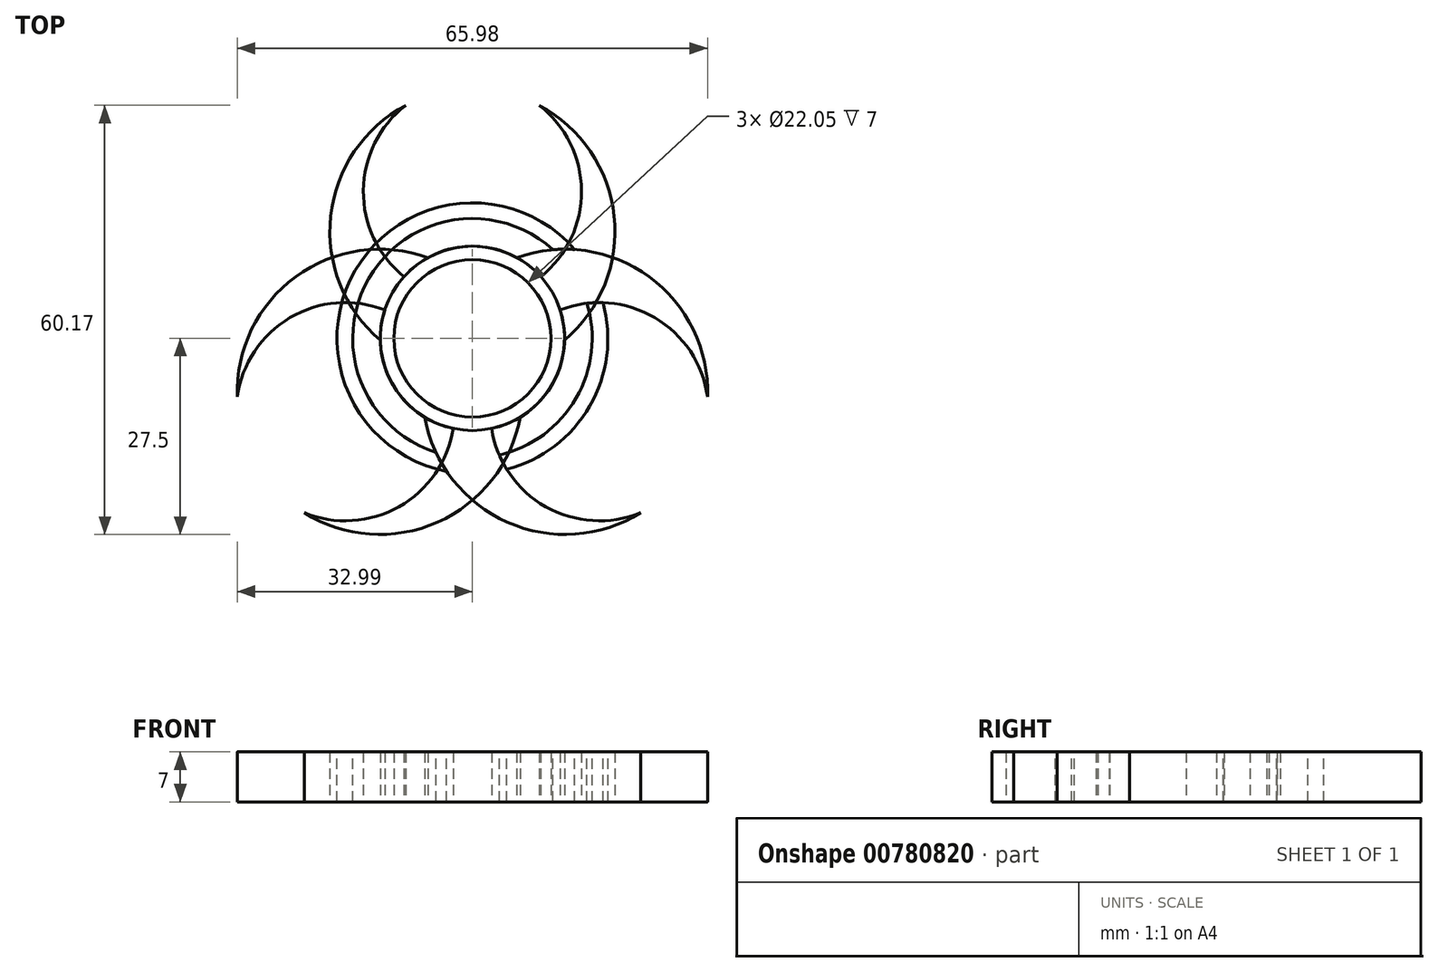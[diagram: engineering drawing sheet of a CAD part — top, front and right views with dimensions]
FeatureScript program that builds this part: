
annotation { "Feature Type Name" : "Feature", "Feature Type Description" : "" }
export const myFeature = defineFeature(function(context is Context, id is Id, definition is map)
    precondition{}
    {
        {
            var Q0;
            Q0=qCreatedBy(makeId("Top.planeOp"),FACE);
            var sketch = newSketch(context, id + "F0", { "sketchPlane" : qUnion([Q0])});
            skCircle(sketch, "E0", {"center": v(0, 0) * mm, "radius": 11.03 * mm});
            skCircle(sketch, "E1.0", {"center": v(0, 0) * mm, "radius": 12.92 * mm});
            skCircle(sketch, "E2", {"center": v(0, 15) * mm, "radius": 20 * mm});
            skLineSegment(sketch, "E3", {"start": v(0, 0) * mm, "end": v(0, -5.23) * mm});
            skCircle(sketch, "E4", {"center": v(0, 20.57) * mm, "radius": 15.3 * mm});
            skSolve(sketch);
        }
        {
            var Q0;
            {var subQ0=sQuery(id+"F0.wireOp",EDGE,"8939bb0d-30df-4b4b-b500-84f4643753330.MirrorC");var subQ1=sQuery(id+"F0.wireOp",EDGE,"E0");var subQ2=makeQuery(id+"F0.imprint","INTERSECT",VERTEX,{"disambiguationData":[OD(0.0)],"derivedFrom":[subQ1,subQ0]});Q0=makeQuery(id+"F0.imprint","IMPRINT",FACE,{"disambiguationData":[TD([[makeQuery(id+"F0.imprint","IMPRINT",EDGE,{"disambiguationData":[TD([[subQ2,-1.0]])],"derivedFrom":subQ1}),-1.0]])]});}
            var Q1;
            {var subQ0=sQuery(id+"F0.wireOp",EDGE,"95fIUpIi-y4c0-pM7q-kLRN-oGn2BKp7xi1O");var subQ1=sQuery(id+"F0.wireOp",EDGE,"E0");var subQ2=makeQuery(id+"F0.imprint","INTERSECT",VERTEX,{"disambiguationData":[OD(1.0)],"derivedFrom":[subQ1,subQ0]});Q1=makeQuery(id+"F0.imprint","IMPRINT",FACE,{"disambiguationData":[TD([[makeQuery(id+"F0.imprint","IMPRINT",EDGE,{"disambiguationData":[TD([[subQ2,-1.0]])],"derivedFrom":subQ1}),-1.0]])]});}
            var Q2;
            {var subQ0=sQuery(id+"F0.wireOp",EDGE,"a428723c-5926-442a-9497-5d29f1fe71100.MirrorC");var subQ1=sQuery(id+"F0.wireOp",EDGE,"E0");var subQ2=makeQuery(id+"F0.imprint","INTERSECT",VERTEX,{"disambiguationData":[OD(0.0)],"derivedFrom":[subQ1,subQ0]});Q2=makeQuery(id+"F0.imprint","IMPRINT",FACE,{"disambiguationData":[TD([[makeQuery(id+"F0.imprint","IMPRINT",EDGE,{"disambiguationData":[TD([[subQ2,1.0]])],"derivedFrom":subQ1}),-1.0]])]});}
            var Q3;
            {var subQ0=sQuery(id+"F0.wireOp",EDGE,"a428723c-5926-442a-9497-5d29f1fe71100.MirrorC");var subQ1=sQuery(id+"F0.wireOp",EDGE,"E0");var subQ2=makeQuery(id+"F0.imprint","INTERSECT",VERTEX,{"disambiguationData":[OD(0.0)],"derivedFrom":[subQ1,subQ0]});Q3=makeQuery(id+"F0.imprint","IMPRINT",FACE,{"disambiguationData":[TD([[makeQuery(id+"F0.imprint","IMPRINT",EDGE,{"disambiguationData":[TD([[subQ2,-1.0]])],"derivedFrom":subQ1}),-1.0]])]});}
            var Q4;
            {var subQ0=sQuery(id+"F0.wireOp",EDGE,"mEyppzmH-Shdz-yvIL-xV5g-pFkc3ElNZCZ9");var subQ1=sQuery(id+"F0.wireOp",EDGE,"E0");var subQ2=makeQuery(id+"F0.imprint","INTERSECT",VERTEX,{"derivedFrom":[subQ1,subQ0]});Q4=makeQuery(id+"F0.imprint","IMPRINT",FACE,{"disambiguationData":[TD([[makeQuery(id+"F0.imprint","IMPRINT",EDGE,{"disambiguationData":[TD([[subQ2,-1.0]])],"derivedFrom":subQ1}),-1.0]])]});}
            var Q5;
            {var subQ0=sQuery(id+"F0.wireOp",EDGE,"95fIUpIi-y4c0-pM7q-kLRN-oGn2BKp7xi1O");var subQ1=sQuery(id+"F0.wireOp",EDGE,"E0");var subQ2=makeQuery(id+"F0.imprint","INTERSECT",VERTEX,{"disambiguationData":[OD(0.0)],"derivedFrom":[subQ1,subQ0]});Q5=makeQuery(id+"F0.imprint","IMPRINT",FACE,{"disambiguationData":[TD([[makeQuery(id+"F0.imprint","IMPRINT",EDGE,{"disambiguationData":[TD([[subQ2,-1.0]])],"derivedFrom":subQ1}),-1.0]])]});}
            var Q6;
            {var subQ0=sQuery(id+"F0.wireOp",EDGE,"1d0d9ce5-5c12-4d60-9ca7-c53f1b6f40260.MirrorC");var subQ1=sQuery(id+"F0.wireOp",EDGE,"E0");var subQ2=makeQuery(id+"F0.imprint","INTERSECT",VERTEX,{"disambiguationData":[OD(1.0)],"derivedFrom":[subQ1,subQ0]});Q6=makeQuery(id+"F0.imprint","IMPRINT",FACE,{"disambiguationData":[TD([[makeQuery(id+"F0.imprint","IMPRINT",EDGE,{"disambiguationData":[TD([[subQ2,-1.0]])],"derivedFrom":subQ1}),-1.0]])]});}
            var Q7;
            {var subQ0=sQuery(id+"F0.wireOp",EDGE,"1rR2SYTX-EKSV-1fxq-I7zs-6o0jOqXutOi4");var subQ1=sQuery(id+"F0.wireOp",EDGE,"E0");var subQ2=makeQuery(id+"F0.imprint","INTERSECT",VERTEX,{"derivedFrom":[subQ1,subQ0]});Q7=makeQuery(id+"F0.imprint","IMPRINT",FACE,{"disambiguationData":[TD([[makeQuery(id+"F0.imprint","IMPRINT",EDGE,{"disambiguationData":[TD([[subQ2,-1.0]])],"derivedFrom":subQ1}),-1.0]])]});}
            var Q8;
            {var subQ0=sQuery(id+"F0.wireOp",EDGE,"a428723c-5926-442a-9497-5d29f1fe71100.MirrorC");var subQ1=sQuery(id+"F0.wireOp",EDGE,"E0");var subQ2=makeQuery(id+"F0.imprint","INTERSECT",VERTEX,{"disambiguationData":[OD(1.0)],"derivedFrom":[subQ1,subQ0]});Q8=makeQuery(id+"F0.imprint","IMPRINT",FACE,{"disambiguationData":[TD([[makeQuery(id+"F0.imprint","IMPRINT",EDGE,{"disambiguationData":[TD([[subQ2,-1.0]])],"derivedFrom":subQ1}),-1.0]])]});}
            var Q9;
            {var subQ0=sQuery(id+"F0.wireOp",EDGE,"1d0d9ce5-5c12-4d60-9ca7-c53f1b6f40260.MirrorC");var subQ1=sQuery(id+"F0.wireOp",EDGE,"E0");var subQ2=makeQuery(id+"F0.imprint","INTERSECT",VERTEX,{"disambiguationData":[OD(0.0)],"derivedFrom":[subQ1,subQ0]});Q9=makeQuery(id+"F0.imprint","IMPRINT",FACE,{"disambiguationData":[TD([[makeQuery(id+"F0.imprint","IMPRINT",EDGE,{"disambiguationData":[TD([[subQ2,1.0]])],"derivedFrom":subQ1}),-1.0]])]});}
            var Q10;
            {var subQ5=sQuery(id+"F0.wireOp",EDGE,"70vgUZuK-qlsv-kuOv-r9a4-axemqHDSPbED");Q10=makeQuery(id+"F0.imprint","IMPRINT",FACE,{"disambiguationData":[TD([[makeQuery(id+"F0.imprint","IMPRINT",EDGE,{"derivedFrom":subQ5}),1.0]])]});}
            var Q11;
            {var subQ5=sQuery(id+"F0.wireOp",EDGE,"d2aa2edc-45a7-4961-bd0e-4b377c2023e90.MirrorCS");Q11=makeQuery(id+"F0.imprint","IMPRINT",FACE,{"disambiguationData":[TD([[makeQuery(id+"F0.imprint","IMPRINT",EDGE,{"derivedFrom":subQ5}),-1.0]])]});}
            var Q12;
            {var subQ0=sQuery(id+"F0.wireOp",EDGE,"E2");var subQ1=sQuery(id+"F0.wireOp",EDGE,"E1.0");var subQ2=makeQuery(id+"F0.imprint","INTERSECT",VERTEX,{"disambiguationData":[OD(0.0)],"derivedFrom":[subQ1,subQ0]});Q12=makeQuery(id+"F0.imprint","IMPRINT",FACE,{"disambiguationData":[TD([[makeQuery(id+"F0.imprint","IMPRINT",EDGE,{"disambiguationData":[TD([[subQ2,1.0]])],"derivedFrom":subQ1}),-1.0]])]});}
            var Q13;
            {var subQ0=sQuery(id+"F0.wireOp",EDGE,"E2");var subQ1=sQuery(id+"F0.wireOp",EDGE,"E1.0");var subQ2=makeQuery(id+"F0.imprint","INTERSECT",VERTEX,{"disambiguationData":[OD(1.0)],"derivedFrom":[subQ1,subQ0]});Q13=makeQuery(id+"F0.imprint","IMPRINT",FACE,{"disambiguationData":[TD([[makeQuery(id+"F0.imprint","IMPRINT",EDGE,{"disambiguationData":[TD([[subQ2,-1.0]])],"derivedFrom":subQ1}),-1.0]])]});}
            extrude(context, id + "F1", {"entities" : qUnion([Q0, Q1, Q2, Q3, Q4, Q5, Q6, Q7, Q8, Q9, Q10, Q11, Q12, Q13]), "depth" : 7 * mm, "offsetDistance" : 25 * mm});
        }
        {
            var Q0;
            Q0=makeQuery(id+"F1.opExtrude","SWEPT_BODY",BODY,{"disambiguationData":[OSD([sQuery(id+"F0.wireOp",EDGE,"E0"),sQuery(id+"F0.wireOp",EDGE,"E1.0"),sQuery(id+"F0.wireOp",EDGE,"E2"),sQuery(id+"F0.wireOp",EDGE,"3RwR9tnb-ImTW-SdPM-kadw-MXWIm4RxCdpV"),sQuery(id+"F0.wireOp",EDGE,"70vgUZuK-qlsv-kuOv-r9a4-axemqHDSPbED"),sQuery(id+"F0.wireOp",EDGE,"d2aa2edc-45a7-4961-bd0e-4b377c2023e90.MirrorCS")])]});
            var Q1;
            {var subQ0=sQuery(id+"F0.wireOp",EDGE,"E2");var subQ1=sQuery(id+"F0.wireOp",EDGE,"E1.0");Q1=makeQuery(id+"F1.opExtrude","SWEPT_FACE",FACE,{"disambiguationData":[OSD([subQ1]),TDD([makeQuery(id+"F0.imprint","IMPRINT",EDGE,{"disambiguationData":[TD([[makeQuery(id+"F0.imprint","INTERSECT",VERTEX,{"disambiguationData":[OD(0.0)],"derivedFrom":[subQ1,subQ0]}),-1.0]])],"derivedFrom":subQ1})])]});}
            circularPattern(context, id + "F2", {"entities" : qUnion([Q0]), "axis" : qUnion([Q1]), "angle" : 360 * degree, "instanceCount" : 3, "equalSpace" : true});
        }
        {
            var Q0;
            Q0=makeQuery(id+"F2.opPattern","COPY",FACE,{"derivedFrom":makeQuery(id+"F1.opExtrude","CAP_FACE",FACE,{"disambiguationData":[OSD([sQuery(id+"F0.wireOp",EDGE,"E0"),sQuery(id+"F0.wireOp",EDGE,"E1.0"),sQuery(id+"F0.wireOp",EDGE,"E2"),sQuery(id+"F0.wireOp",EDGE,"3RwR9tnb-ImTW-SdPM-kadw-MXWIm4RxCdpV"),sQuery(id+"F0.wireOp",EDGE,"70vgUZuK-qlsv-kuOv-r9a4-axemqHDSPbED"),sQuery(id+"F0.wireOp",EDGE,"d2aa2edc-45a7-4961-bd0e-4b377c2023e90.MirrorCS")])],"isStart":false}),"instanceName":"1"});
            var sketch = newSketch(context, id + "F3", { "sketchPlane" : qUnion([Q0])});
            skCircle(sketch, "E5", {"center": v(0, 0) * mm, "radius": 16.8 * mm});
            skCircle(sketch, "E6", {"center": v(0, 0) * mm, "radius": 19 * mm});
            skSolve(sketch);
        }
        {
            var Q0;
            {var subQ0=sQuery(id+"F3.wireOp",EDGE,"9C3PVVKS-q9cu-0s60-txqP-e2Dki8VLNxZq");var subQ1=sQuery(id+"F0.wireOp",EDGE,"E2");var subQ3=makeQuery(id+"F2.opPattern","COPY",EDGE,{"derivedFrom":makeQuery(id+"F1.opExtrude","CAP_EDGE",EDGE,{"disambiguationData":[OSD([subQ1]),TDD([makeQuery(id+"F0.imprint","IMPRINT",EDGE,{"disambiguationData":[TD([[makeQuery(id+"F0.imprint","INTERSECT",VERTEX,{"derivedFrom":[subQ1,sQuery(id+"F0.wireOp",EDGE,"70vgUZuK-qlsv-kuOv-r9a4-axemqHDSPbED")]}),-1.0]])],"derivedFrom":subQ1})])],"isStart":false}),"instanceName":"1"});var subQ4=makeQuery(id+"F3.imprint","INTERSECT",VERTEX,{"derivedFrom":[subQ3,subQ0]});Q0=makeQuery(id+"F3.imprint","IMPRINT",FACE,{"disambiguationData":[TD([[makeQuery(id+"F3.imprint","IMPRINT",EDGE,{"disambiguationData":[TD([[subQ4,-1.0]])],"derivedFrom":subQ0}),-1.0]])]});}
            var Q1;
            {var subQ0=sQuery(id+"F3.wireOp",EDGE,"9C3PVVKS-q9cu-0s60-txqP-e2Dki8VLNxZq");var subQ1=sQuery(id+"F0.wireOp",EDGE,"3RwR9tnb-ImTW-SdPM-kadw-MXWIm4RxCdpV");var subQ3=makeQuery(id+"F2.opPattern","COPY",EDGE,{"derivedFrom":makeQuery(id+"F1.opExtrude","CAP_EDGE",EDGE,{"disambiguationData":[OSD([subQ1]),TDD([makeQuery(id+"F0.imprint","IMPRINT",EDGE,{"disambiguationData":[TD([[makeQuery(id+"F0.imprint","INTERSECT",VERTEX,{"derivedFrom":[subQ1,sQuery(id+"F0.wireOp",EDGE,"70vgUZuK-qlsv-kuOv-r9a4-axemqHDSPbED")]}),-1.0]])],"derivedFrom":subQ1})])],"isStart":false}),"instanceName":"1"});var subQ4=makeQuery(id+"F3.imprint","INTERSECT",VERTEX,{"derivedFrom":[subQ3,subQ0]});Q1=makeQuery(id+"F3.imprint","IMPRINT",FACE,{"disambiguationData":[TD([[makeQuery(id+"F3.imprint","IMPRINT",EDGE,{"disambiguationData":[TD([[subQ4,1.0]])],"derivedFrom":subQ0}),-1.0]])]});}
            var Q2;
            {var subQ0=sQuery(id+"F3.wireOp",EDGE,"9C3PVVKS-q9cu-0s60-txqP-e2Dki8VLNxZq");var subQ1=sQuery(id+"F0.wireOp",EDGE,"d2aa2edc-45a7-4961-bd0e-4b377c2023e90.MirrorCS");var subQ2=sQuery(id+"F0.wireOp",EDGE,"E2");var subQ4=makeQuery(id+"F2.opPattern","COPY",EDGE,{"derivedFrom":makeQuery(id+"F1.opExtrude","CAP_EDGE",EDGE,{"disambiguationData":[OSD([subQ2]),TDD([makeQuery(id+"F0.imprint","IMPRINT",EDGE,{"disambiguationData":[TD([[makeQuery(id+"F0.imprint","INTERSECT",VERTEX,{"derivedFrom":[subQ2,subQ1]}),1.0]])],"derivedFrom":subQ2})])],"isStart":false}),"instanceName":"1"});var subQ5=makeQuery(id+"F3.imprint","INTERSECT",VERTEX,{"derivedFrom":[subQ4,subQ0]});Q2=makeQuery(id+"F3.imprint","IMPRINT",FACE,{"disambiguationData":[TD([[makeQuery(id+"F3.imprint","IMPRINT",EDGE,{"disambiguationData":[TD([[subQ5,-1.0]])],"derivedFrom":subQ0}),-1.0]])]});}
            var Q3;
            {var subQ0=sQuery(id+"F3.wireOp",EDGE,"9C3PVVKS-q9cu-0s60-txqP-e2Dki8VLNxZq");var subQ1=sQuery(id+"F0.wireOp",EDGE,"70vgUZuK-qlsv-kuOv-r9a4-axemqHDSPbED");var subQ2=sQuery(id+"F0.wireOp",EDGE,"E2");var subQ4=makeQuery(id+"F2.opPattern","COPY",EDGE,{"derivedFrom":makeQuery(id+"F1.opExtrude","CAP_EDGE",EDGE,{"disambiguationData":[OSD([subQ2]),TDD([makeQuery(id+"F0.imprint","IMPRINT",EDGE,{"disambiguationData":[TD([[makeQuery(id+"F0.imprint","INTERSECT",VERTEX,{"derivedFrom":[subQ2,subQ1]}),-1.0]])],"derivedFrom":subQ2})])],"isStart":false}),"instanceName":"1"});var subQ5=makeQuery(id+"F3.imprint","INTERSECT",VERTEX,{"derivedFrom":[subQ4,subQ0]});Q3=makeQuery(id+"F3.imprint","IMPRINT",FACE,{"disambiguationData":[TD([[makeQuery(id+"F3.imprint","IMPRINT",EDGE,{"disambiguationData":[TD([[subQ5,1.0]])],"derivedFrom":subQ0}),-1.0]])]});}
            var Q4;
            {var subQ0=sQuery(id+"F3.wireOp",EDGE,"xcDpeXkk-nX5Y-ApxZ-C3hR-QqdVYPBwRqQI");var subQ1=sQuery(id+"F0.wireOp",EDGE,"E2");var subQ2=sQuery(id+"F0.wireOp",EDGE,"E1.0");var subQ4=makeQuery(id+"F2.opPattern","COPY",EDGE,{"derivedFrom":makeQuery(id+"F1.opExtrude","CAP_EDGE",EDGE,{"disambiguationData":[OSD([subQ1]),TDD([makeQuery(id+"F0.imprint","IMPRINT",EDGE,{"disambiguationData":[TD([[makeQuery(id+"F0.imprint","INTERSECT",VERTEX,{"disambiguationData":[OD(0.0)],"derivedFrom":[subQ2,subQ1]}),1.0]])],"derivedFrom":subQ1})])],"isStart":false}),"instanceName":"1"});var subQ5=makeQuery(id+"F3.imprint","INTERSECT",VERTEX,{"derivedFrom":[subQ4,subQ0]});Q4=makeQuery(id+"F3.imprint","IMPRINT",FACE,{"disambiguationData":[TD([[makeQuery(id+"F3.imprint","IMPRINT",EDGE,{"disambiguationData":[TD([[subQ5,-1.0]])],"derivedFrom":subQ0}),1.0]])]});}
            var Q5;
            {var subQ0=sQuery(id+"F3.wireOp",EDGE,"xcDpeXkk-nX5Y-ApxZ-C3hR-QqdVYPBwRqQI");var subQ1=sQuery(id+"F0.wireOp",EDGE,"E4");var subQ2=sQuery(id+"F0.wireOp",EDGE,"E2");var subQ4=makeQuery(id+"F2.opPattern","COPY",EDGE,{"derivedFrom":makeQuery(id+"F1.opExtrude","CAP_EDGE",EDGE,{"disambiguationData":[OSD([subQ1]),TDD([makeQuery(id+"F0.imprint","IMPRINT",EDGE,{"disambiguationData":[TD([[makeQuery(id+"F0.imprint","INTERSECT",VERTEX,{"disambiguationData":[OD(0.0)],"derivedFrom":[subQ2,subQ1]}),-1.0]])],"derivedFrom":subQ1})])],"isStart":false}),"instanceName":"1"});var subQ5=makeQuery(id+"F3.imprint","INTERSECT",VERTEX,{"derivedFrom":[subQ4,subQ0]});Q5=makeQuery(id+"F3.imprint","IMPRINT",FACE,{"disambiguationData":[TD([[makeQuery(id+"F3.imprint","IMPRINT",EDGE,{"disambiguationData":[TD([[subQ5,1.0]])],"derivedFrom":subQ0}),1.0]])]});}
            var Q6;
            {var subQ0=sQuery(id+"F3.wireOp",EDGE,"9jYISCpo-EIcX-wsJ9-kGUm-02aJbQ1Lkd42");var subQ1=sQuery(id+"F0.wireOp",EDGE,"E2");var subQ2=sQuery(id+"F0.wireOp",EDGE,"E1.0");var subQ4=makeQuery(id+"F2.opPattern","COPY",EDGE,{"derivedFrom":makeQuery(id+"F1.opExtrude","CAP_EDGE",EDGE,{"disambiguationData":[OSD([subQ1]),TDD([makeQuery(id+"F0.imprint","IMPRINT",EDGE,{"disambiguationData":[TD([[makeQuery(id+"F0.imprint","INTERSECT",VERTEX,{"disambiguationData":[OD(0.0)],"derivedFrom":[subQ2,subQ1]}),1.0]])],"derivedFrom":subQ1})])],"isStart":false}),"instanceName":"1"});var subQ5=makeQuery(id+"F3.imprint","INTERSECT",VERTEX,{"derivedFrom":[subQ4,subQ0]});Q6=makeQuery(id+"F3.imprint","IMPRINT",FACE,{"disambiguationData":[TD([[makeQuery(id+"F3.imprint","IMPRINT",EDGE,{"disambiguationData":[TD([[subQ5,-1.0]])],"derivedFrom":subQ0}),-1.0]])]});}
            var Q7;
            {var subQ0=sQuery(id+"F3.wireOp",EDGE,"9jYISCpo-EIcX-wsJ9-kGUm-02aJbQ1Lkd42");var subQ1=sQuery(id+"F0.wireOp",EDGE,"E4");var subQ2=sQuery(id+"F0.wireOp",EDGE,"E2");var subQ4=makeQuery(id+"F2.opPattern","COPY",EDGE,{"derivedFrom":makeQuery(id+"F1.opExtrude","CAP_EDGE",EDGE,{"disambiguationData":[OSD([subQ1]),TDD([makeQuery(id+"F0.imprint","IMPRINT",EDGE,{"disambiguationData":[TD([[makeQuery(id+"F0.imprint","INTERSECT",VERTEX,{"disambiguationData":[OD(0.0)],"derivedFrom":[subQ2,subQ1]}),-1.0]])],"derivedFrom":subQ1})])],"isStart":false}),"instanceName":"1"});var subQ5=makeQuery(id+"F3.imprint","INTERSECT",VERTEX,{"derivedFrom":[subQ4,subQ0]});Q7=makeQuery(id+"F3.imprint","IMPRINT",FACE,{"disambiguationData":[TD([[makeQuery(id+"F3.imprint","IMPRINT",EDGE,{"disambiguationData":[TD([[subQ5,1.0]])],"derivedFrom":subQ0}),-1.0]])]});}
            var Q8;
            {var subQ0=sQuery(id+"F3.wireOp",EDGE,"E5");var subQ1=sQuery(id+"F0.wireOp",EDGE,"E2");var subQ2=sQuery(id+"F0.wireOp",EDGE,"E1.0");var subQ4=makeQuery(id+"F2.opPattern","COPY",EDGE,{"derivedFrom":makeQuery(id+"F1.opExtrude","CAP_EDGE",EDGE,{"disambiguationData":[OSD([subQ1]),TDD([makeQuery(id+"F0.imprint","IMPRINT",EDGE,{"disambiguationData":[TD([[makeQuery(id+"F0.imprint","INTERSECT",VERTEX,{"disambiguationData":[OD(0.0)],"derivedFrom":[subQ2,subQ1]}),1.0]])],"derivedFrom":subQ1})])],"isStart":false}),"instanceName":"1"});var subQ5=makeQuery(id+"F3.imprint","INTERSECT",VERTEX,{"derivedFrom":[subQ4,subQ0]});Q8=makeQuery(id+"F3.imprint","IMPRINT",FACE,{"disambiguationData":[TD([[makeQuery(id+"F3.imprint","IMPRINT",EDGE,{"disambiguationData":[TD([[subQ5,-1.0]])],"derivedFrom":subQ0}),-1.0]])]});}
            var Q9;
            {var subQ0=sQuery(id+"F3.wireOp",EDGE,"E5");var subQ1=sQuery(id+"F0.wireOp",EDGE,"E4");var subQ2=sQuery(id+"F0.wireOp",EDGE,"E2");var subQ4=makeQuery(id+"F2.opPattern","COPY",EDGE,{"derivedFrom":makeQuery(id+"F1.opExtrude","CAP_EDGE",EDGE,{"disambiguationData":[OSD([subQ1]),TDD([makeQuery(id+"F0.imprint","IMPRINT",EDGE,{"disambiguationData":[TD([[makeQuery(id+"F0.imprint","INTERSECT",VERTEX,{"disambiguationData":[OD(0.0)],"derivedFrom":[subQ2,subQ1]}),-1.0]])],"derivedFrom":subQ1})])],"isStart":false}),"instanceName":"1"});var subQ5=makeQuery(id+"F3.imprint","INTERSECT",VERTEX,{"derivedFrom":[subQ4,subQ0]});Q9=makeQuery(id+"F3.imprint","IMPRINT",FACE,{"disambiguationData":[TD([[makeQuery(id+"F3.imprint","IMPRINT",EDGE,{"disambiguationData":[TD([[subQ5,1.0]])],"derivedFrom":subQ0}),-1.0]])]});}
            extrude(context, id + "F4", {"entities" : qUnion([Q0, Q1, Q2, Q3, Q4, Q5, Q6, Q7, Q8, Q9]), "oppositeDirection" : true, "depth" : 7 * mm, "offsetDistance" : 25 * mm});
        }
    });
